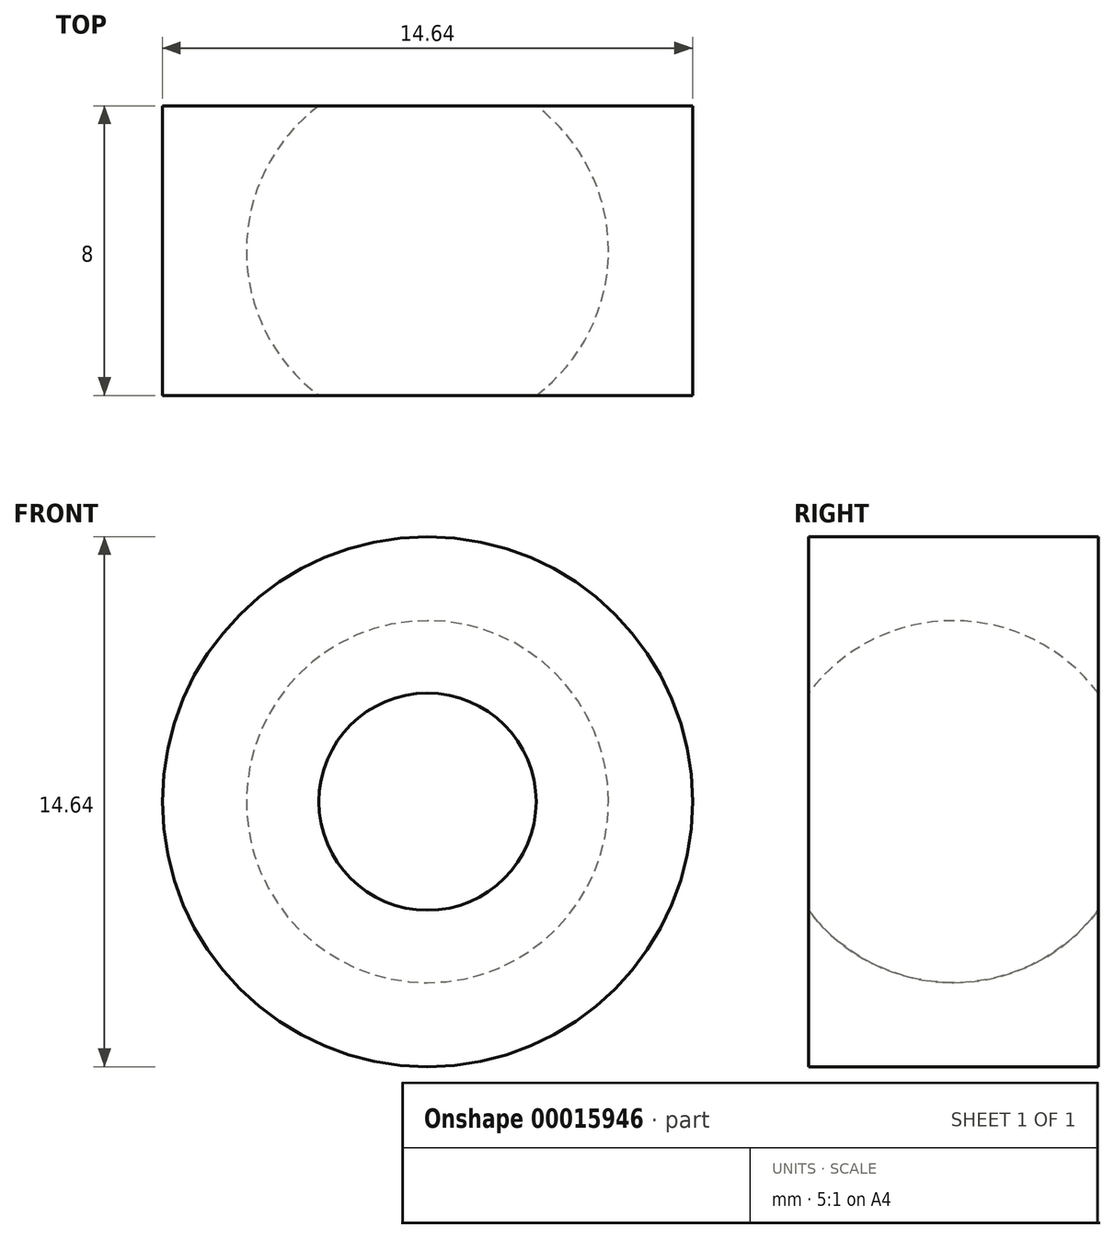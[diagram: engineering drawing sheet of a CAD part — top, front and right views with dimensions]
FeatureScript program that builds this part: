
annotation { "Feature Type Name" : "Feature", "Feature Type Description" : "" }
export const myFeature = defineFeature(function(context is Context, id is Id, definition is map)
    precondition{}
    {
        {
            var Q0;
            Q0=qCreatedBy(makeId("Top.planeOp"),FACE);
            var sketch = newSketch(context, id + "F0", { "sketchPlane" : qUnion([Q0])});
            skCircle(sketch, "E0", {"center": v(0, 0) * mm, "radius": 5 * mm});
            skLineSegment(sketch, "E1", {"start": v(0, 5) * mm, "end": v(0, -5) * mm});
            skLineSegment(sketch, "E2.bottom", {"start": v(-8.5, 5) * mm, "end": v(1.5, 5) * mm});
            skLineSegment(sketch, "E2.top", {"start": v(-8.5, -5) * mm, "end": v(1.5, -5) * mm});
            skLineSegment(sketch, "E2.left", {"start": v(-8.5, 5) * mm, "end": v(-8.5, -5) * mm});
            skLineSegment(sketch, "E2.right", {"start": v(1.5, 5) * mm, "end": v(1.5, -5) * mm});
            skPoint(sketch, "E3", {"position": v(-8.5, 0) * mm});
            skLineSegment(sketch, "E4", {"start": v(0, 0.75) * mm, "end": v(1.5, 0.75) * mm, "construction": true});
            skSolve(sketch);
        }
        {
            var Q0;
            {var subQ0=sQuery(id+"F0.wireOp",EDGE,"E2.right");var subQ1=sQuery(id+"F0.wireOp",EDGE,"E0");var subQ3=makeQuery(id+"F0.imprint","INTERSECT",VERTEX,{"disambiguationData":[OD(0.0)],"derivedFrom":[subQ1,subQ0]});Q0=makeQuery(id+"F0.imprint","IMPRINT",FACE,{"disambiguationData":[TD([[makeQuery(id+"F0.imprint","IMPRINT",EDGE,{"disambiguationData":[TD([[subQ3,1.0]])],"derivedFrom":subQ1}),1.0]])]});}
            var Q1;
            Q1=sQuery(id+"F0.wireOp",EDGE,"E1");
            revolve(context, id + "F1", {"entities" : qUnion([Q0]), "axis" : qUnion([Q1]), "revolveType" : RevolveType.FULL});
        }
        {
            var Q0;
            Q0=qCreatedBy(makeId("Front.planeOp"),FACE);
            var sketch = newSketch(context, id + "F2", { "sketchPlane" : qUnion([Q0])});
            skCircle(sketch, "E5", {"center": v(0, 0) * mm, "radius": 7.32 * mm});
            skSolve(sketch);
        }
        {
            var Q0;
            Q0=makeQuery(id+"F2.imprint","IMPRINT",FACE,{"disambiguationData":[TD([[makeQuery(id+"F2.imprint","IMPRINT",EDGE,{"derivedFrom":sQuery(id+"F2.wireOp",EDGE,"E5")}),1.0]])]});
            extrude(context, id + "F3", {"entities" : qUnion([Q0]), "depth" : 8 * mm, "symmetric" : true});
        }
        {
            var Q0;
            {var subQ0=sQuery(id+"F0.wireOp",EDGE,"E2.right");var subQ1=sQuery(id+"F0.wireOp",EDGE,"E0");var subQ3=makeQuery(id+"F0.imprint","INTERSECT",VERTEX,{"disambiguationData":[OD(0.0)],"derivedFrom":[subQ1,subQ0]});Q0=makeQuery(id+"F0.imprint","IMPRINT",FACE,{"disambiguationData":[TD([[makeQuery(id+"F0.imprint","IMPRINT",EDGE,{"disambiguationData":[TD([[subQ3,1.0]])],"derivedFrom":subQ1}),1.0]])]});}
            var Q1;
            {var subQ4=sQuery(id+"F0.wireOp",EDGE,"E1");Q1=makeQuery(id+"F0.imprint","IMPRINT",FACE,{"disambiguationData":[TD([[makeQuery(id+"F0.imprint","IMPRINT",EDGE,{"derivedFrom":subQ4}),1.0]])]});}
            var Q2;
            Q2=sQuery(id+"F0.wireOp",EDGE,"E1");
            revolve(context, id + "F4", {"operationType" : NewBodyOperationType.REMOVE, "entities" : qUnion([Q0, Q1]), "axis" : qUnion([Q2]), "revolveType" : RevolveType.FULL, "oppositeDirection" : true});
        }
    });
